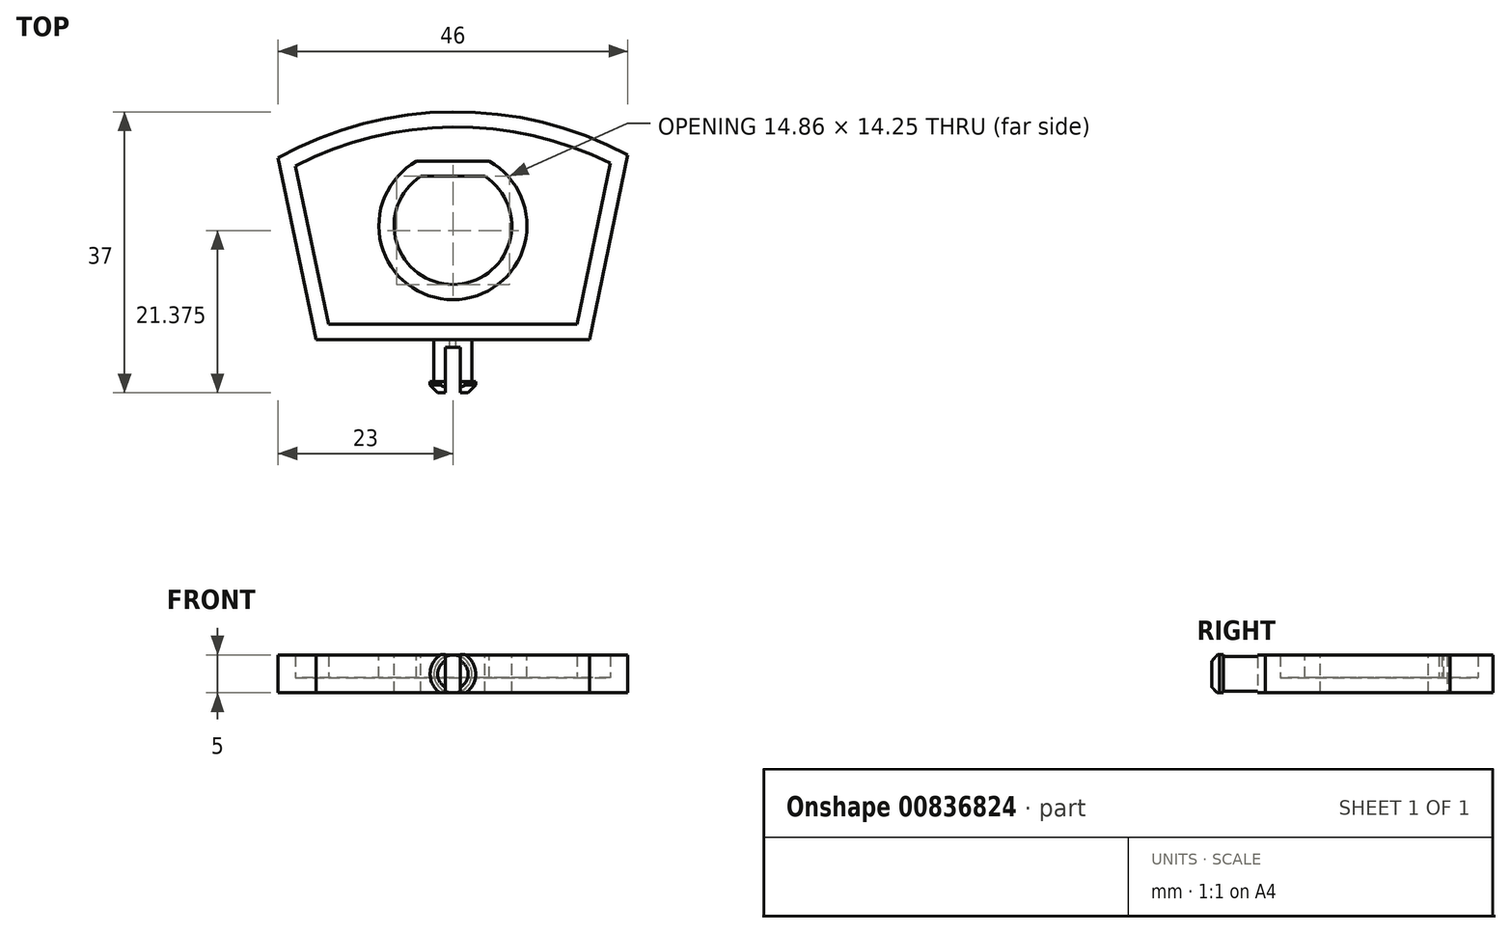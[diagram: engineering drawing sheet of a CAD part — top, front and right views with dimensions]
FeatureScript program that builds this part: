
annotation { "Feature Type Name" : "Feature", "Feature Type Description" : "" }
export const myFeature = defineFeature(function(context is Context, id is Id, definition is map)
    precondition{}
    {
        {
            var Q0;
            Q0=qCreatedBy(makeId("Top.planeOp"),FACE);
            var sketch = newSketch(context, id + "F0", { "sketchPlane" : qUnion([Q0])});
            skLineSegment(sketch, "E0", {"start": v(-23, 23.93) * mm, "end": v(-18, 0) * mm});
            skLineSegment(sketch, "E1", {"start": v(-18, 0) * mm, "end": v(18, 0) * mm});
            skLineSegment(sketch, "E2", {"start": v(18, 0) * mm, "end": v(23, 24.33) * mm});
            skArc(sketch, "E3", {"start": v(23, 24.33) * mm, "mid": v(-0.05, 30) * mm, "end": v(-23, 23.93) * mm});
            skSolve(sketch);
        }
        {
            var Q0;
            Q0=makeQuery(id+"F0.imprint","IMPRINT",FACE,{"disambiguationData":[TD([[makeQuery(id+"F0.imprint","IMPRINT",EDGE,{"derivedFrom":sQuery(id+"F0.wireOp",EDGE,"E0")}),1.0]])]});
            extrude(context, id + "F1", {"entities" : qUnion([Q0]), "endBound" : BoundingType.SYMMETRIC, "depth" : 5 * mm, "offsetDistance" : 25 * mm});
        }
        {
            var Q0;
            Q0=makeQuery(id+"F1.opExtrude","CAP_FACE",FACE,{"disambiguationData":[OSD([sQuery(id+"F0.wireOp",EDGE,"E0"),sQuery(id+"F0.wireOp",EDGE,"E1"),sQuery(id+"F0.wireOp",EDGE,"E2"),sQuery(id+"F0.wireOp",EDGE,"E3")])],"isStart":false});
            var sketch = newSketch(context, id + "F2", { "sketchPlane" : qUnion([Q0])});
            skLineSegment(sketch, "E4", {"start": v(-4.22, 21.5) * mm, "end": v(4.22, 21.5) * mm});
            skArc(sketch, "E5", {"start": v(-4.22, 21.5) * mm, "mid": v(0, 7.25) * mm, "end": v(4.22, 21.5) * mm});
            skSolve(sketch);
        }
        {
            var Q0;
            Q0 = qSketchRegion(id + "F2", true);
            extrude(context, id + "F3", {"entities" : qUnion([Q0]), "operationType" : NewBodyOperationType.REMOVE, "endBound" : BoundingType.UP_TO_NEXT, "oppositeDirection" : true, "depth" : 25 * mm, "offsetDistance" : 25 * mm});
        }
        {
            var Q0;
            Q0=makeQuery(id+"F1.opExtrude","CAP_FACE",FACE,{"disambiguationData":[OSD([sQuery(id+"F0.wireOp",EDGE,"E0"),sQuery(id+"F0.wireOp",EDGE,"E1"),sQuery(id+"F0.wireOp",EDGE,"E2"),sQuery(id+"F0.wireOp",EDGE,"E3")])],"isStart":false});
            shell(context, id + "F4", {"entities" : qUnion([Q0]), "thickness" : 2 * mm});
        }
        {
            var Q0;
            Q0=qCreatedBy(makeId("Right.planeOp"),FACE);
            var sketch = newSketch(context, id + "F5", { "sketchPlane" : qUnion([Q0])});
            skLineSegment(sketch, "E6", {"start": v(0, 0) * mm, "end": v(-7, 0) * mm});
            skLineSegment(sketch, "E7", {"start": v(-7, 0) * mm, "end": v(-7, 3) * mm});
            skLineSegment(sketch, "E8", {"start": v(-7, 3) * mm, "end": v(-5.5, 3) * mm});
            skLineSegment(sketch, "E9", {"start": v(-5.5, 3) * mm, "end": v(-5.5, 2.5) * mm});
            skLineSegment(sketch, "E10", {"start": v(-5.5, 2.5) * mm, "end": v(0, 2.5) * mm});
            skLineSegment(sketch, "E11", {"start": v(0, 2.5) * mm, "end": v(0, 0) * mm});
            skSolve(sketch);
        }
        {
            var Q0;
            Q0=makeQuery(id+"F5.imprint","IMPRINT",FACE,{"disambiguationData":[TD([[makeQuery(id+"F5.imprint","IMPRINT",EDGE,{"derivedFrom":sQuery(id+"F5.wireOp",EDGE,"E6")}),-1.0]])]});
            var Q1;
            Q1=sQuery(id+"F5.wireOp",EDGE,"E6");
            revolve(context, id + "F6", {"operationType" : NewBodyOperationType.ADD, "surfaceOperationType" : NewSurfaceOperationType.NEW, "entities" : qUnion([Q0]), "axis" : qUnion([Q1]), "revolveType" : RevolveType.FULL});
        }
        {
            var Q0;
            Q0=makeQuery(id+"F6.opRevolve","SWEPT_EDGE",EDGE,{"disambiguationData":[OSD([sQuery(id+"F5.wireOp",EDGE,"E7"),sQuery(id+"F5.wireOp",EDGE,"E8")])]});
            chamfer(context, id + "F7", {"entities" : qUnion([Q0]), "width" : 1 * mm, "tangentPropagation" : true});
        }
        {
            var Q0;
            Q0=makeQuery(id+"F6.opRevolve","SWEPT_FACE",FACE,{"disambiguationData":[OSD([sQuery(id+"F5.wireOp",EDGE,"E7")])]});
            var sketch = newSketch(context, id + "F8", { "sketchPlane" : qUnion([Q0])});
            skLineSegment(sketch, "E12.bottom", {"start": v(-28.39, 2.53) * mm, "end": v(27.18, 2.53) * mm});
            skLineSegment(sketch, "E12.top", {"start": v(-28.39, -2.47) * mm, "end": v(27.18, -2.47) * mm});
            skLineSegment(sketch, "E12.left", {"start": v(-28.39, 2.53) * mm, "end": v(-28.39, -2.47) * mm});
            skLineSegment(sketch, "E12.right", {"start": v(27.18, 2.53) * mm, "end": v(27.18, -2.47) * mm});
            skSolve(sketch);
        }
        {
            var Q0;
            Q0 = qSketchRegion(id + "F8", true);
            extrude(context, id + "F9", {"entities" : qUnion([Q0]), "operationType" : NewBodyOperationType.INTERSECT, "endBound" : BoundingType.THROUGH_ALL, "oppositeDirection" : true, "depth" : 25 * mm, "offsetDistance" : 25 * mm});
        }
        {
            var Q0;
            Q0=makeQuery(id+"F6.opRevolve","SWEPT_FACE",FACE,{"disambiguationData":[OSD([sQuery(id+"F5.wireOp",EDGE,"E7")])]});
            var sketch = newSketch(context, id + "F10", { "sketchPlane" : qUnion([Q0])});
            skLineSegment(sketch, "E13.bottom", {"start": v(-1, 3.4) * mm, "end": v(1, 3.4) * mm});
            skLineSegment(sketch, "E13.top", {"start": v(-1, -4.47) * mm, "end": v(1, -4.47) * mm});
            skLineSegment(sketch, "E13.left", {"start": v(-1, 3.4) * mm, "end": v(-1, -4.47) * mm});
            skLineSegment(sketch, "E13.right", {"start": v(1, 3.4) * mm, "end": v(1, -4.47) * mm});
            skSolve(sketch);
        }
        {
            var Q0;
            Q0 = qSketchRegion(id + "F10", true);
            extrude(context, id + "F11", {"entities" : qUnion([Q0]), "operationType" : NewBodyOperationType.REMOVE, "oppositeDirection" : true, "depth" : 6 * mm, "offsetDistance" : 25 * mm});
        }
    });
